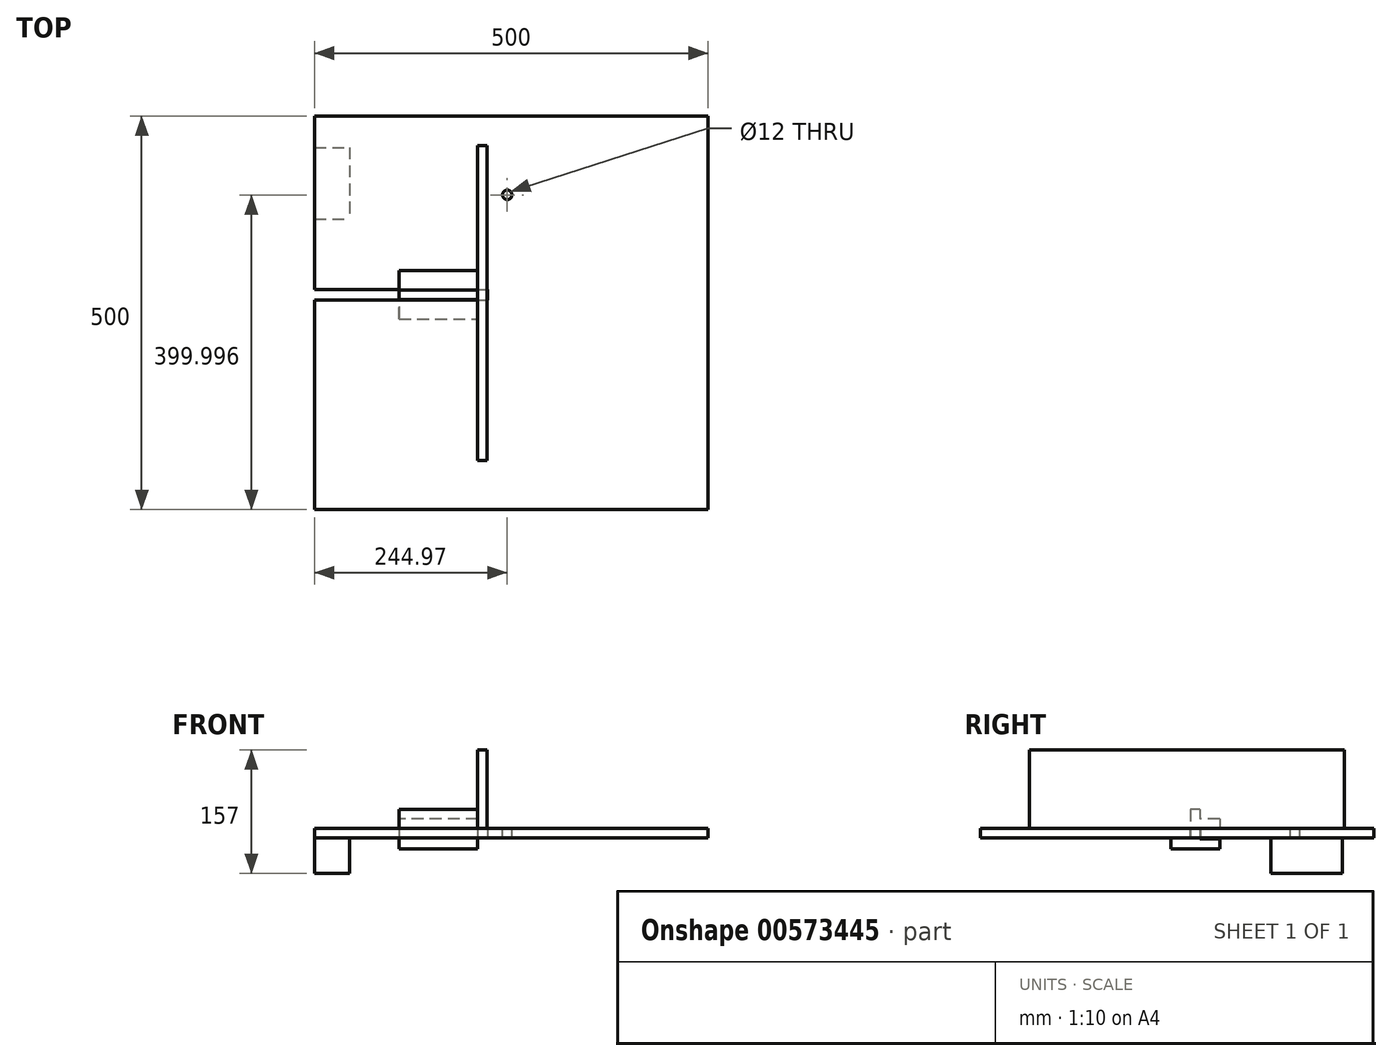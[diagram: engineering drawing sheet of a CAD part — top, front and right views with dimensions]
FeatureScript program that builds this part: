
annotation { "Feature Type Name" : "Feature", "Feature Type Description" : "" }
export const myFeature = defineFeature(function(context is Context, id is Id, definition is map)
    precondition{}
    {
        {
            var Q0;
            Q0=qCreatedBy(makeId("Top.planeOp"),FACE);
            var sketch = newSketch(context, id + "F0", { "sketchPlane" : qUnion([Q0])});
            skLineSegment(sketch, "E0.bottom", {"start": v(-244.97, 249.46) * mm, "end": v(255.03, 249.46) * mm});
            skLineSegment(sketch, "E0.top", {"start": v(-244.97, -250.54) * mm, "end": v(255.03, -250.54) * mm});
            skLineSegment(sketch, "E0.left", {"start": v(-244.97, 249.46) * mm, "end": v(-244.97, -250.54) * mm});
            skLineSegment(sketch, "E0.right", {"start": v(255.03, 249.46) * mm, "end": v(255.03, -250.54) * mm});
            skLineSegment(sketch, "E1.bottom", {"start": v(-244.97, 29.1) * mm, "end": v(-24.97, 29.1) * mm});
            skLineSegment(sketch, "E1.top", {"start": v(-244.97, 16.1) * mm, "end": v(-24.97, 16.1) * mm});
            skLineSegment(sketch, "E1.left", {"start": v(-244.97, 29.1) * mm, "end": v(-244.97, 16.1) * mm});
            skLineSegment(sketch, "E1.right", {"start": v(-24.97, 29.1) * mm, "end": v(-24.97, 16.1) * mm});
            skSolve(sketch);
        }
        {
            var Q0;
            Q0=makeQuery(id+"F0.imprint","IMPRINT",FACE,{"disambiguationData":[TD([[makeQuery(id+"F0.imprint","IMPRINT",EDGE,{"derivedFrom":sQuery(id+"F0.wireOp",EDGE,"E0.bottom")}),-1.0]])]});
            extrude(context, id + "F1", {"entities" : qUnion([Q0]), "depth" : 12 * mm, "offsetDistance" : 25 * mm});
        }
        {
            var Q0;
            Q0=makeQuery(id+"F1.opExtrude","CAP_FACE",FACE,{"disambiguationData":[OSD([sQuery(id+"F0.wireOp",EDGE,"E0.bottom"),sQuery(id+"F0.wireOp",EDGE,"E0.top"),sQuery(id+"F0.wireOp",EDGE,"E0.left"),sQuery(id+"F0.wireOp",EDGE,"E0.right"),sQuery(id+"F0.wireOp",EDGE,"E1.bottom"),sQuery(id+"F0.wireOp",EDGE,"E1.top"),sQuery(id+"F0.wireOp",EDGE,"E1.right")])],"isStart":false});
            var sketch = newSketch(context, id + "F2", { "sketchPlane" : qUnion([Q0])});
            skLineSegment(sketch, "E2", {"start": v(0, 0) * mm, "end": v(0, 249.46) * mm});
            skPoint(sketch, "E3", {"position": v(0, 149.46) * mm});
            skSolve(sketch);
        }
        {
            var Q0;
            Q0=sQuery(id+"F2.wireOp",VERTEX,"E3");
            var Q1;
            Q1=makeQuery(id+"F1.opExtrude","SWEPT_BODY",BODY,{"disambiguationData":[OSD([sQuery(id+"F0.wireOp",EDGE,"E0.bottom"),sQuery(id+"F0.wireOp",EDGE,"E0.top"),sQuery(id+"F0.wireOp",EDGE,"E0.left"),sQuery(id+"F0.wireOp",EDGE,"E0.right"),sQuery(id+"F0.wireOp",EDGE,"E1.bottom"),sQuery(id+"F0.wireOp",EDGE,"E1.top"),sQuery(id+"F0.wireOp",EDGE,"E1.right")])]});
            hole(context, id + "F3", {"style" : HoleStyle.SIMPLE, "endStyle" : HoleEndStyle.THROUGH, "holeDiameter" : 12 * mm, "isTappedThrough" : true, "tappedDepth" : 12 * mm, "tapClearance" : 3, "locations" : qUnion([Q0]), "scope" : qUnion([Q1])});
        }
        {
            var Q0;
            Q0=makeQuery(id+"F1.opExtrude","CAP_FACE",FACE,{"disambiguationData":[OSD([sQuery(id+"F0.wireOp",EDGE,"E0.bottom"),sQuery(id+"F0.wireOp",EDGE,"E0.top"),sQuery(id+"F0.wireOp",EDGE,"E0.left"),sQuery(id+"F0.wireOp",EDGE,"E0.right"),sQuery(id+"F0.wireOp",EDGE,"E1.bottom"),sQuery(id+"F0.wireOp",EDGE,"E1.top"),sQuery(id+"F0.wireOp",EDGE,"E1.right")])],"isStart":false});
            var sketch = newSketch(context, id + "F4", { "sketchPlane" : qUnion([Q0])});
            skLineSegment(sketch, "E4.bottom", {"start": v(-37.42, 211.8) * mm, "end": v(-25.42, 211.8) * mm});
            skLineSegment(sketch, "E4.top", {"start": v(-37.42, -188.2) * mm, "end": v(-25.42, -188.2) * mm});
            skLineSegment(sketch, "E4.left", {"start": v(-37.42, 211.8) * mm, "end": v(-37.42, -188.2) * mm});
            skLineSegment(sketch, "E4.right", {"start": v(-25.42, 211.8) * mm, "end": v(-25.42, -188.2) * mm});
            skSolve(sketch);
        }
        {
            var Q0;
            Q0 = qSketchRegion(id + "F4", true);
            extrude(context, id + "F5", {"entities" : qUnion([Q0]), "depth" : 100 * mm, "offsetDistance" : 25 * mm});
        }
        {
            var Q0;
            Q0=makeQuery(id+"F5.opExtrude","SWEPT_FACE",FACE,{"disambiguationData":[OSD([sQuery(id+"F4.wireOp",EDGE,"E4.left")])]});
            var sketch = newSketch(context, id + "F6", { "sketchPlane" : qUnion([Q0])});
            skLineSegment(sketch, "E5.bottom", {"start": v(-28.6, 36) * mm, "end": v(-16.6, 36) * mm});
            skLineSegment(sketch, "E5.top", {"start": v(-28.6, -14) * mm, "end": v(-16.6, -14) * mm});
            skLineSegment(sketch, "E5.left", {"start": v(-28.6, 36) * mm, "end": v(-28.6, -14) * mm});
            skLineSegment(sketch, "E5.right", {"start": v(-16.6, 36) * mm, "end": v(-16.6, -14) * mm});
            skSolve(sketch);
        }
        {
            var Q0;
            Q0 = qSketchRegion(id + "F6", true);
            extrude(context, id + "F7", {"entities" : qUnion([Q0]), "operationType" : NewBodyOperationType.ADD, "depth" : 100 * mm, "offsetDistance" : 25 * mm});
        }
        {
            var Q0;
            Q0=makeQuery(id+"F7.opExtrude","SWEPT_FACE",FACE,{"disambiguationData":[OSD([sQuery(id+"F6.wireOp",EDGE,"E5.right")])]});
            var sketch = newSketch(context, id + "F8", { "sketchPlane" : qUnion([Q0])});
            skLineSegment(sketch, "E6.bottom", {"start": v(-137.42, -14) * mm, "end": v(-37.42, -14) * mm});
            skLineSegment(sketch, "E6.top", {"start": v(-137.42, 0) * mm, "end": v(-37.42, 0) * mm});
            skLineSegment(sketch, "E6.left", {"start": v(-137.42, -14) * mm, "end": v(-137.42, 0) * mm});
            skLineSegment(sketch, "E6.right", {"start": v(-37.42, -14) * mm, "end": v(-37.42, 0) * mm});
            skSolve(sketch);
        }
        {
            var Q0;
            Q0 = qSketchRegion(id + "F8", true);
            extrude(context, id + "F9", {"entities" : qUnion([Q0]), "operationType" : NewBodyOperationType.ADD, "depth" : 25 * mm, "offsetDistance" : 25 * mm});
        }
        {
            var Q0;
            Q0=makeQuery(id+"F7.opExtrude","SWEPT_FACE",FACE,{"disambiguationData":[OSD([sQuery(id+"F6.wireOp",EDGE,"E5.left")])]});
            var sketch = newSketch(context, id + "F10", { "sketchPlane" : qUnion([Q0])});
            skPoint(sketch, "E7.oppositeSnap0", {"position": v(37.42, -1) * mm});
            skLineSegment(sketch, "E7.bottom", {"start": v(37.42, -14) * mm, "end": v(137.42, -14) * mm});
            skLineSegment(sketch, "E7.top", {"start": v(37.42, -1) * mm, "end": v(137.42, -1) * mm});
            skLineSegment(sketch, "E7.left", {"start": v(37.42, -14) * mm, "end": v(37.42, -1) * mm});
            skLineSegment(sketch, "E7.right", {"start": v(137.42, -14) * mm, "end": v(137.42, -1) * mm});
            skSolve(sketch);
        }
        {
            var Q0;
            Q0 = qSketchRegion(id + "F10", true);
            extrude(context, id + "F11", {"entities" : qUnion([Q0]), "operationType" : NewBodyOperationType.ADD, "depth" : 25 * mm, "offsetDistance" : 25 * mm});
        }
        {
            var Q0;
            Q0=makeQuery(id+"F7.opExtrude","SWEPT_FACE",FACE,{"disambiguationData":[OSD([sQuery(id+"F6.wireOp",EDGE,"E5.left")])]});
            var sketch = newSketch(context, id + "F12", { "sketchPlane" : qUnion([Q0])});
            skLineSegment(sketch, "E8.bottom", {"start": v(37.42, 12) * mm, "end": v(137.42, 12) * mm});
            skLineSegment(sketch, "E8.top", {"start": v(37.42, 24) * mm, "end": v(137.42, 24) * mm});
            skLineSegment(sketch, "E8.left", {"start": v(37.42, 12) * mm, "end": v(37.42, 24) * mm});
            skLineSegment(sketch, "E8.right", {"start": v(137.42, 12) * mm, "end": v(137.42, 24) * mm});
            skSolve(sketch);
        }
        {
            var Q0;
            Q0 = qSketchRegion(id + "F12", true);
            extrude(context, id + "F13", {"entities" : qUnion([Q0]), "operationType" : NewBodyOperationType.ADD, "depth" : 25 * mm, "offsetDistance" : 25 * mm});
        }
        {
            var Q0;
            Q0=makeQuery(id+"F1.opExtrude","CAP_FACE",FACE,{"disambiguationData":[OSD([sQuery(id+"F0.wireOp",EDGE,"E0.bottom"),sQuery(id+"F0.wireOp",EDGE,"E0.top"),sQuery(id+"F0.wireOp",EDGE,"E0.left"),sQuery(id+"F0.wireOp",EDGE,"E0.right"),sQuery(id+"F0.wireOp",EDGE,"E1.bottom"),sQuery(id+"F0.wireOp",EDGE,"E1.top"),sQuery(id+"F0.wireOp",EDGE,"E1.right")])],"isStart":true});
            var sketch = newSketch(context, id + "F14", { "sketchPlane" : qUnion([Q0])});
            skLineSegment(sketch, "E9.bottom", {"start": v(-244.97, -209.75) * mm, "end": v(-199.97, -209.75) * mm});
            skLineSegment(sketch, "E9.top", {"start": v(-244.97, -118.67) * mm, "end": v(-199.97, -118.67) * mm});
            skLineSegment(sketch, "E9.left", {"start": v(-244.97, -209.75) * mm, "end": v(-244.97, -118.67) * mm});
            skLineSegment(sketch, "E9.right", {"start": v(-199.97, -209.75) * mm, "end": v(-199.97, -118.67) * mm});
            skSolve(sketch);
        }
        {
            var Q0;
            Q0=makeQuery(id+"F14.imprint","IMPRINT",FACE,{"disambiguationData":[TD([[makeQuery(id+"F14.imprint","IMPRINT",EDGE,{"derivedFrom":sQuery(id+"F14.wireOp",EDGE,"E9.bottom")}),1.0]])]});
            extrude(context, id + "F15", {"entities" : qUnion([Q0]), "depth" : 45 * mm, "offsetDistance" : 25 * mm});
        }
    });
